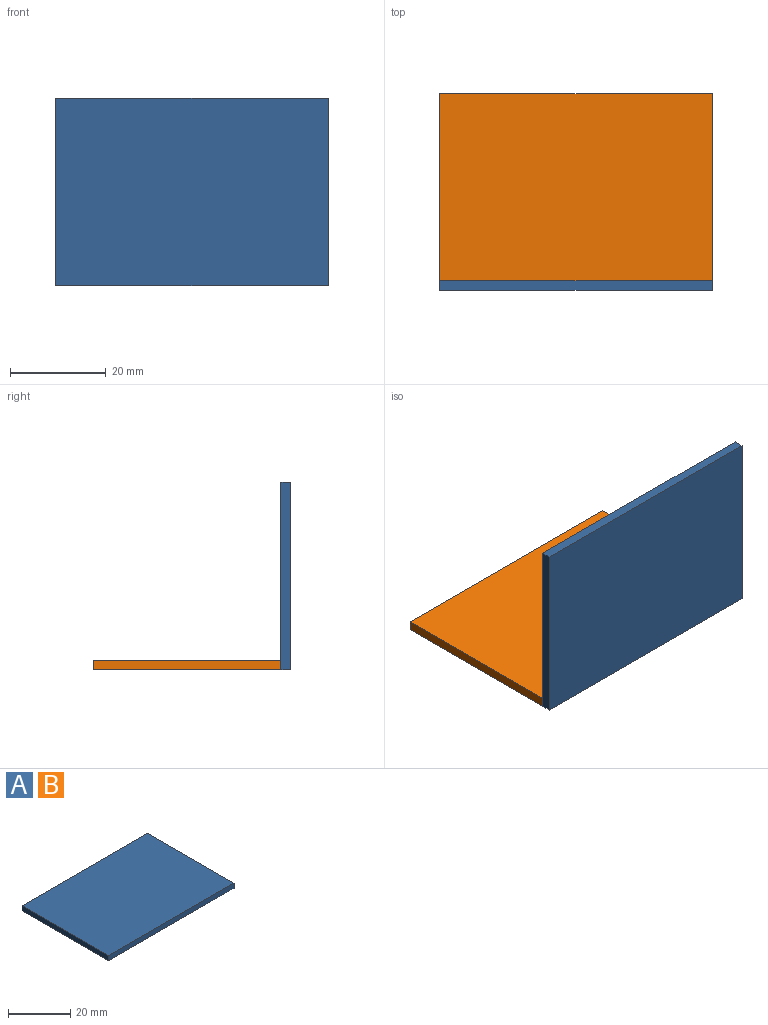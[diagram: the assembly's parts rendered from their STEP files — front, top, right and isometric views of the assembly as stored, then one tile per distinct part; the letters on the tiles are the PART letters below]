
ASSEMBLY  parts=2 mates=1
PART A: 6 faces, bbox 56.9x39.1x2 mm
  f0: plane 56.88x2mm, normal (0,1,0), area 113.8mm2, adj f1,f3,f4,f5
  f1: plane 39.11x2mm, normal (-1,0,0), area 78.2mm2, adj f0,f2,f4,f5
  f2: plane 56.88x2mm, normal (0,-1,0), area 113.8mm2, adj f1,f3,f4,f5
  f3: plane 39.11x2mm, normal (1,0,0), area 78.2mm2, adj f0,f2,f4,f5
  f4: plane 56.88x39.11mm, normal (0,0,1), area 2224.7mm2, adj f0,f1,f2,f3
  f5: plane 56.88x39.11mm, normal (0,0,-1), area 2224.7mm2, adj f0,f1,f2,f3
PART B: same geometry as A
PLACE A rot(axis=(1,0,0),90deg) t=(0,0,0)mm
PLACE B at identity
MATE fastened A.f2 <-> B.f5  axis (0,0,-1) through (0,0,0)mm
